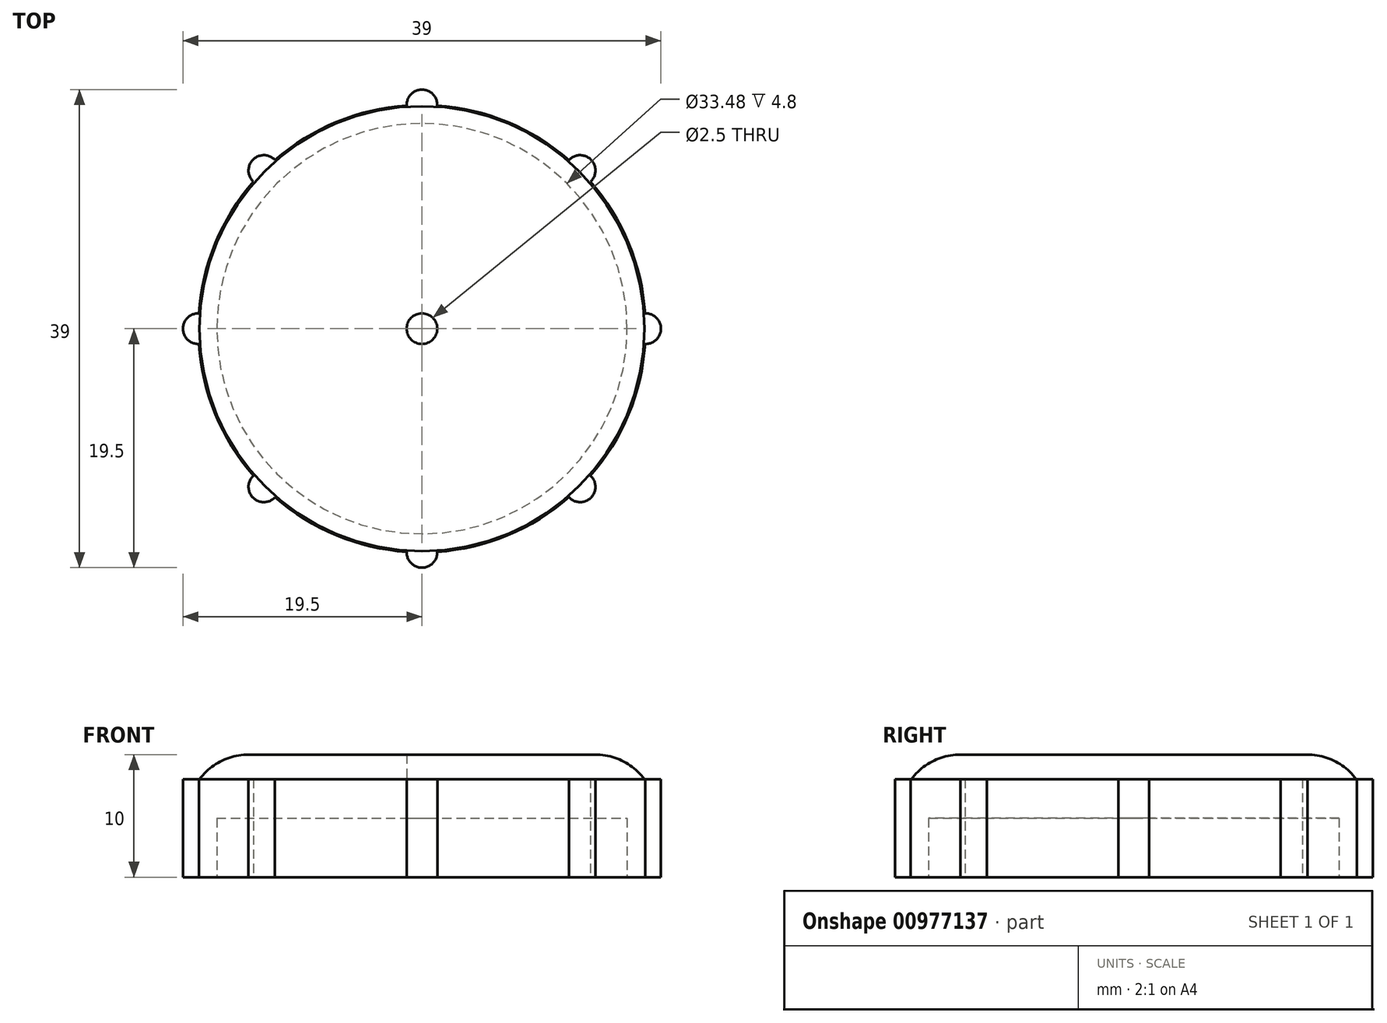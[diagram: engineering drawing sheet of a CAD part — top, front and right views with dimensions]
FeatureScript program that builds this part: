
annotation { "Feature Type Name" : "Feature", "Feature Type Description" : "" }
export const myFeature = defineFeature(function(context is Context, id is Id, definition is map)
    precondition{}
    {
        {
            var Q0;
            Q0=qCreatedBy(makeId("Top.planeOp"),FACE);
            var sketch = newSketch(context, id + "F0", { "sketchPlane" : qUnion([Q0])});
            skCircle(sketch, "E0", {"center": v(0, 0) * mm, "radius": 18.25 * mm});
            skCircle(sketch, "E1", {"center": v(0, 18.25) * mm, "radius": 1.25 * mm});
            skCircle(sketch, "E2.1.0", {"center": v(-12.9, 12.9) * mm, "radius": 1.25 * mm});
            skCircle(sketch, "E2.2.0", {"center": v(-18.25, 0) * mm, "radius": 1.25 * mm});
            skCircle(sketch, "E2.3.0", {"center": v(-12.9, -12.9) * mm, "radius": 1.25 * mm});
            skCircle(sketch, "E2.4.0", {"center": v(0, -18.25) * mm, "radius": 1.25 * mm});
            skCircle(sketch, "E2.5.0", {"center": v(12.9, -12.9) * mm, "radius": 1.25 * mm});
            skCircle(sketch, "E2.6.0", {"center": v(18.25, 0) * mm, "radius": 1.25 * mm});
            skCircle(sketch, "E2.7.0", {"center": v(12.9, 12.9) * mm, "radius": 1.25 * mm});
            skSolve(sketch);
        }
        {
            var Q0;
            Q0 = qSketchRegion(id + "F0", true);
            extrude(context, id + "F1", {"entities" : qUnion([Q0]), "depth" : 8 * mm, "offsetDistance" : 25 * mm});
        }
        {
            var Q0;
            Q0=makeQuery(id+"F1.opExtrude","CAP_FACE",FACE,{"disambiguationData":[OSD([sQuery(id+"F0.wireOp",EDGE,"E1"),sQuery(id+"F0.wireOp",EDGE,"E2.1.0"),sQuery(id+"F0.wireOp",EDGE,"E2.2.0"),sQuery(id+"F0.wireOp",EDGE,"E2.3.0"),sQuery(id+"F0.wireOp",EDGE,"E2.4.0"),sQuery(id+"F0.wireOp",EDGE,"E2.5.0"),sQuery(id+"F0.wireOp",EDGE,"E2.6.0"),sQuery(id+"F0.wireOp",EDGE,"E2.7.0"),sQuery(id+"F0.wireOp",EDGE,"E0")])],"isStart":true});
            var sketch = newSketch(context, id + "F2", { "sketchPlane" : qUnion([Q0])});
            skCircle(sketch, "E3", {"center": v(0, 0) * mm, "radius": 16.74 * mm});
            skSolve(sketch);
        }
        {
            var Q0;
            Q0 = qSketchRegion(id + "F2", true);
            extrude(context, id + "F3", {"entities" : qUnion([Q0]), "operationType" : NewBodyOperationType.REMOVE, "oppositeDirection" : true, "depth" : 4.8 * mm, "offsetDistance" : 25 * mm});
        }
        {
            var Q0;
            Q0=makeQuery(id+"F1.opExtrude","CAP_FACE",FACE,{"disambiguationData":[OSD([sQuery(id+"F0.wireOp",EDGE,"E1"),sQuery(id+"F0.wireOp",EDGE,"E2.1.0"),sQuery(id+"F0.wireOp",EDGE,"E2.2.0"),sQuery(id+"F0.wireOp",EDGE,"E2.3.0"),sQuery(id+"F0.wireOp",EDGE,"E2.4.0"),sQuery(id+"F0.wireOp",EDGE,"E2.5.0"),sQuery(id+"F0.wireOp",EDGE,"E2.6.0"),sQuery(id+"F0.wireOp",EDGE,"E2.7.0"),sQuery(id+"F0.wireOp",EDGE,"E0")])],"isStart":false});
            var sketch = newSketch(context, id + "F4", { "sketchPlane" : qUnion([Q0])});
            skCircle(sketch, "E4", {"center": v(0, 0) * mm, "radius": 18.15 * mm});
            skSolve(sketch);
        }
        {
            var Q0;
            Q0 = qSketchRegion(id + "F4", true);
            extrude(context, id + "F5", {"entities" : qUnion([Q0]), "operationType" : NewBodyOperationType.ADD, "depth" : 2 * mm, "offsetDistance" : 25 * mm});
        }
        {
            var Q0;
            Q0=makeQuery(id+"F5.opExtrude","CAP_EDGE",EDGE,{"disambiguationData":[OSD([sQuery(id+"F4.wireOp",EDGE,"E4")])],"isStart":false});
            fillet(context, id + "F6", {"entities" : qUnion([Q0]), "radius" : 5 * mm, "tangentPropagation" : true, "allowEdgeOverflow" : false});
        }
        {
            var Q0;
            Q0=makeQuery(id+"F3.boolean.opBoolean","COPY",FACE,{"derivedFrom":makeQuery(id+"F3.opExtrude","CAP_FACE",FACE,{"disambiguationData":[OSD([sQuery(id+"F2.wireOp",EDGE,"E3")])],"isStart":false})});
            var sketch = newSketch(context, id + "F7", { "sketchPlane" : qUnion([Q0])});
            skCircle(sketch, "E5", {"center": v(0, 0) * mm, "radius": 1.25 * mm});
            skSolve(sketch);
        }
        {
            var Q0;
            Q0 = qSketchRegion(id + "F7", true);
            extrude(context, id + "F8", {"entities" : qUnion([Q0]), "operationType" : NewBodyOperationType.REMOVE, "oppositeDirection" : true, "depth" : 25 * mm, "offsetDistance" : 25 * mm});
        }
    });
